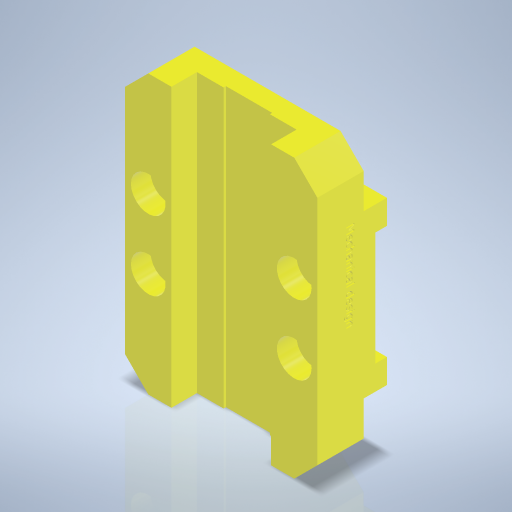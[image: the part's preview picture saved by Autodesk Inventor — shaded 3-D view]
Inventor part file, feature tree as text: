
AUTODESK INVENTOR PART (.ipt)
format: ipt  version: 2024 (Build 280153000, 153)  size: 730,624 bytes
history: native  units: mm
features: sketch x6, extrude x4, projected_geometry x4, chamfer x1, hole x1, plane x1, mirror x1, other x1
ambient origin geometry x8: Origin, YZ Plane, XZ Plane, XY Plane, X Axis, Y Axis, Z Axis, Center Point
bodies: Volumenkörper1 (feature_tree)
feature tree (19):
  extrude  "Extrusion1"  Depth=83.0mm
  extrude  "Extrusion2"  Depth=2.0mm TaperAngle=45.0deg
  chamfer  "Fasen1"  Distance=20.0mm
  extrude  "Extrusion3"  Depth=1.0mm TaperAngle=0.0deg
  extrude  "Extrusion4"  Depth=1.0mm
  hole  "Bohrung1"  [1 undecoded]
  plane  "Arbeitsebene1"
  mirror  "Spiegeln1"
  other  "Prägen1"
  sketch  "Skizze1"  dims[d3=0.0mm d6=83.0mm]
  sketch  "Skizze2"  dims[d8=0.0mm d10=2.0mm d11=45.0deg]
  sketch  "Skizze3"  dims[d12=11.0mm]
  projected_geometry  "Projizierte Kontur1"
  projected_geometry  "Projizierte Kontur2"
  projected_geometry  "Projizierte Kontur3"
  projected_geometry  "Projizierte Kontur4"
  sketch  "Skizze4"  dims[d13=12.0mm]
  sketch  "Skizze6"  dims[d14=10.0mm]
  sketch  "Skizze7"  dims[d15=10.0mm d16=20.0mm d17=10.0mm d18=0.0mm d19=49.0mm d20=10.5mm d22=4.0mm d23=4.0mm d24=5.0mm d25=0.0mm d27=30.0mm d28=9.0mm d29=6.0mm d30=15.0mm d31=8.5mm d32=90.0deg d33=12.5mm d34=20.594885mm d35=-41.5mm d36=10.131585mm d37=6.0mm d38=20.0mm d39=17.0mm d40=1.0mm d41=0.0mm]
note: 1 required parameter value undecoded (feature->parameter linkage not recoverable at this tier; creation-order binding heuristic only, values carry confidence <= 0.55)
